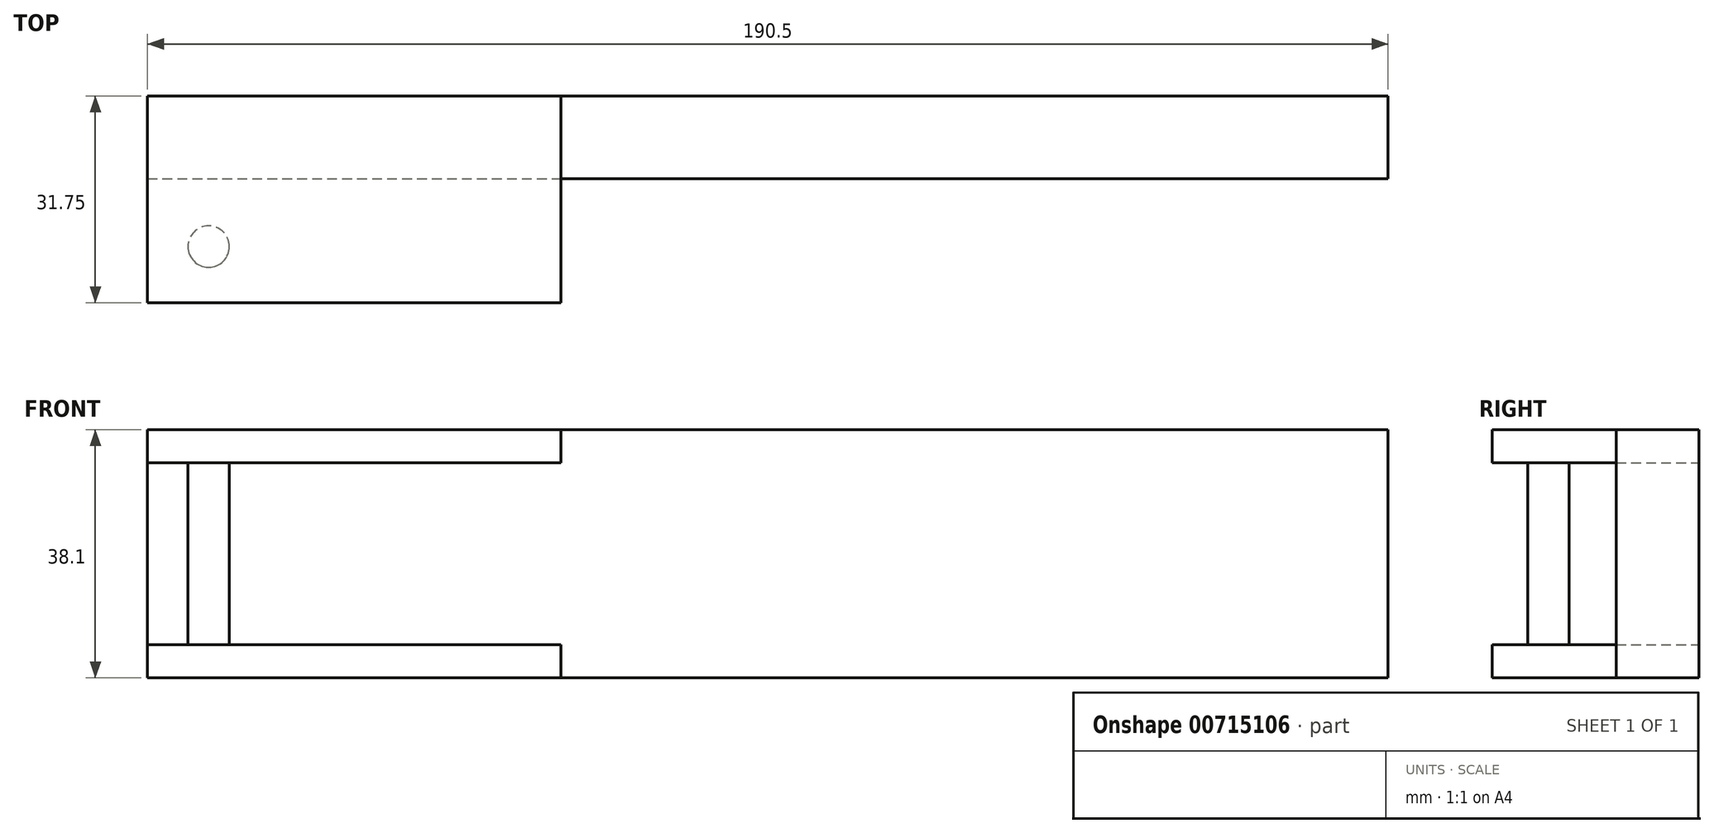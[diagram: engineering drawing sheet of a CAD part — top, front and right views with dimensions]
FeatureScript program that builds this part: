
annotation { "Feature Type Name" : "Feature", "Feature Type Description" : "" }
export const myFeature = defineFeature(function(context is Context, id is Id, definition is map)
    precondition{}
    {
        {
            var Q0;
            Q0=qCreatedBy(makeId("Front.planeOp"),FACE);
            var sketch = newSketch(context, id + "F0", { "sketchPlane" : qUnion([Q0])});
            skLineSegment(sketch, "E0.bottom", {"start": v(95.25, 19.05) * mm, "end": v(-95.25, 19.05) * mm});
            skLineSegment(sketch, "E0.top", {"start": v(95.25, -19.05) * mm, "end": v(-95.25, -19.05) * mm});
            skLineSegment(sketch, "E0.left", {"start": v(95.25, 19.05) * mm, "end": v(95.25, -19.05) * mm});
            skLineSegment(sketch, "E0.right", {"start": v(-95.25, 19.05) * mm, "end": v(-95.25, -19.05) * mm});
            skPoint(sketch, "E0.middle", {"position": v(0, 0) * mm});
            skLineSegment(sketch, "E1", {"start": v(-31.75, -19.05) * mm, "end": v(-31.75, 19.05) * mm});
            skLineSegment(sketch, "E2", {"start": v(-95.25, 13.97) * mm, "end": v(-31.75, 13.97) * mm});
            skLineSegment(sketch, "E3", {"start": v(-95.25, -13.97) * mm, "end": v(-31.75, -13.97) * mm});
            skSolve(sketch);
        }
        {
            var Q0;
            {var subQ5=sQuery(id+"F0.wireOp",EDGE,"E2");Q0=makeQuery(id+"F0.imprint","IMPRINT",FACE,{"disambiguationData":[TD([[makeQuery(id+"F0.imprint","IMPRINT",EDGE,{"derivedFrom":subQ5}),1.0]])]});}
            var Q1;
            {var subQ5=sQuery(id+"F0.wireOp",EDGE,"E3");Q1=makeQuery(id+"F0.imprint","IMPRINT",FACE,{"disambiguationData":[TD([[makeQuery(id+"F0.imprint","IMPRINT",EDGE,{"derivedFrom":subQ5}),-1.0]])]});}
            extrude(context, id + "F1", {"entities" : qUnion([Q0, Q1]), "depth" : 31.75 * mm, "offsetDistance" : 25.4 * mm});
        }
        {
            var Q0;
            {var subQ0=sQuery(id+"F0.wireOp",EDGE,"E2");Q0=makeQuery(id+"F0.imprint","IMPRINT",FACE,{"disambiguationData":[TD([[makeQuery(id+"F0.imprint","IMPRINT",EDGE,{"derivedFrom":subQ0}),-1.0]])]});}
            var Q1;
            {var subQ4=sQuery(id+"F0.wireOp",EDGE,"E0.left");Q1=makeQuery(id+"F0.imprint","IMPRINT",FACE,{"disambiguationData":[TD([[makeQuery(id+"F0.imprint","IMPRINT",EDGE,{"derivedFrom":subQ4}),-1.0]])]});}
            extrude(context, id + "F2", {"entities" : qUnion([Q0, Q1]), "depth" : 12.7 * mm, "offsetDistance" : 25.4 * mm});
        }
        {
            var Q0;
            Q0=makeQuery(id+"F1.opExtrude","SWEPT_FACE",FACE,{"disambiguationData":[OSD([sQuery(id+"F0.wireOp",EDGE,"E2")])]});
            var sketch = newSketch(context, id + "F3", { "sketchPlane" : qUnion([Q0])});
            skCircle(sketch, "E4", {"center": v(-85.85, 23.12) * mm, "radius": 3.18 * mm});
            skSolve(sketch);
        }
        {
            var Q0;
            Q0=makeQuery(id+"F3.imprint","IMPRINT",FACE,{"disambiguationData":[TD([[makeQuery(id+"F3.imprint","IMPRINT",EDGE,{"derivedFrom":sQuery(id+"F3.wireOp",EDGE,"E4")}),1.0]])]});
            extrude(context, id + "F4", {"entities" : qUnion([Q0]), "operationType" : NewBodyOperationType.ADD, "depth" : 28.7 * mm, "offsetDistance" : 25.4 * mm});
        }
    });
